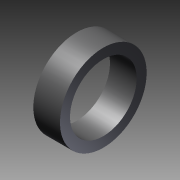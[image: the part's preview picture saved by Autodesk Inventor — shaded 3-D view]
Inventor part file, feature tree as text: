
AUTODESK INVENTOR PART (.ipt)
format: ipt  version: 2011 SP1 (Build 150282100, 282)  size: 84,992 bytes
history: native  units: mm
features: other x7, revolve x1, sketch x1
ambient origin geometry x8: Origin, YZ Plane, XZ Plane, XY Plane, X Axis, Y Axis, Z Axis, Center Point
bodies: Solid1 (feature_tree)
feature tree (9):
  revolve  "Revolution1"  [1 undecoded]
  other  "collar_XY"
  other  "collar_YZ"
  other  "collar_ZX"
  other  "collar_X"
  other  "collar_Y"
  other  "collar_Z"
  other  "collar_Center"
  sketch  "Sketch_1"  dims[d0=360.0deg d1=0.0mm]
note: 1 required parameter value undecoded (feature->parameter linkage not recoverable at this tier; creation-order binding heuristic only, values carry confidence <= 0.55)
